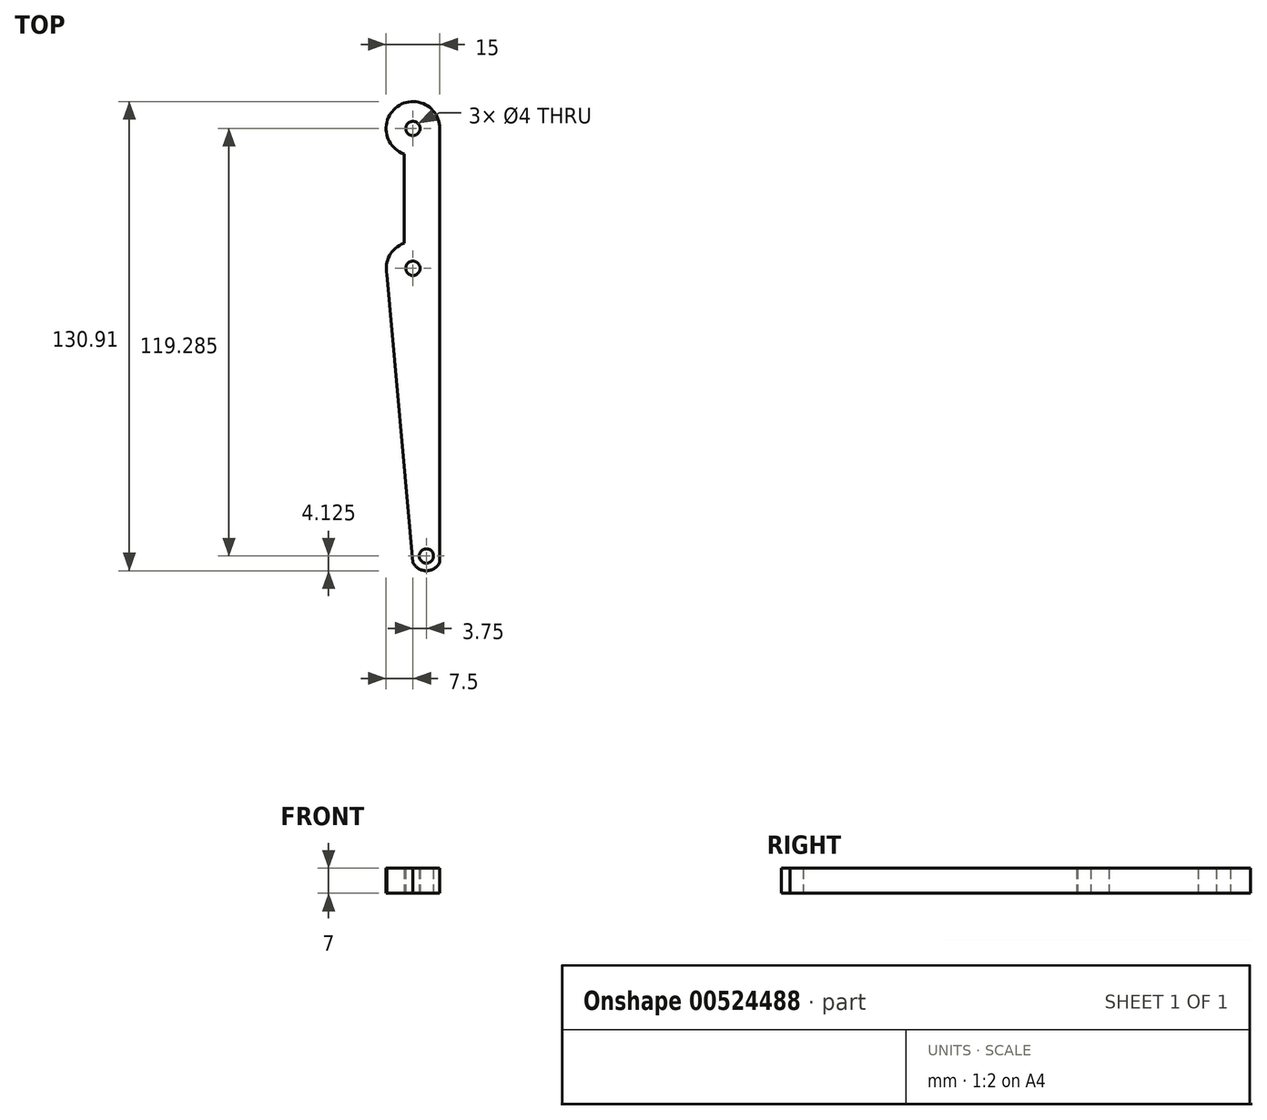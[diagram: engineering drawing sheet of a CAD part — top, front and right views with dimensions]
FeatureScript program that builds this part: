
annotation { "Feature Type Name" : "Feature", "Feature Type Description" : "" }
export const myFeature = defineFeature(function(context is Context, id is Id, definition is map)
    precondition{}
    {
        {
            var Q0;
            Q0=qCreatedBy(makeId("Top.planeOp"),FACE);
            var sketch = newSketch(context, id + "F0", { "sketchPlane" : qUnion([Q0])});
            skArc(sketch, "E0", {"start": v(7.5, 0) * mm, "mid": v(-4.33, 6.12) * mm, "end": v(-2.5, -7.07) * mm});
            skLineSegment(sketch, "E1.top", {"start": v(7.5, -41) * mm, "end": v(7.16, -41) * mm});
            skLineSegment(sketch, "E1.left", {"start": v(7.5, 0) * mm, "end": v(7.5, -41) * mm});
            skLineSegment(sketch, "E1.right", {"start": v(-2.5, -7.07) * mm, "end": v(-2.5, -32.01) * mm});
            skArc(sketch, "E2", {"start": v(-2.5, -32.01) * mm, "mid": v(-6.54, -35.48) * mm, "end": v(-7.22, -40.77) * mm});
            skPoint(sketch, "E3.start.orphan", {"position": v(0, -0.9) * mm});
            skLineSegment(sketch, "E4", {"start": v(7.5, -41) * mm, "end": v(7.5, -121) * mm});
            skPoint(sketch, "E5.second.point", {"position": v(0, -121) * mm});
            skPoint(sketch, "E5.third.point", {"position": v(1.86, -115.62) * mm});
            skLineSegment(sketch, "E6", {"start": v(-7.22, -40.77) * mm, "end": v(0, -121) * mm});
            skCircle(sketch, "E7", {"center": v(3.75, -119.28) * mm, "radius": 2 * mm});
            skArc(sketch, "E8.trimOffspring", {"start": v(0, -121) * mm, "mid": v(3.75, -123.4) * mm, "end": v(7.5, -121) * mm});
            skSolve(sketch);
        }
        {
            var Q0;
            Q0=makeQuery(id+"F0.imprint","IMPRINT",FACE,{"disambiguationData":[TD([[makeQuery(id+"F0.imprint","IMPRINT",EDGE,{"derivedFrom":sQuery(id+"F0.wireOp",EDGE,"E0")}),1.0]])]});
            extrude(context, id + "F1", {"entities" : qUnion([Q0]), "depth" : 7 * mm, "offsetDistance" : 25 * mm});
        }
        {
            var Q0;
            Q0=sQuery(id+"F0.wireOp",VERTEX,"E0.center");
            var Q1;
            Q1=makeQuery(id+"F1.opExtrude","SWEPT_BODY",BODY,{"disambiguationData":[OSD([sQuery(id+"F0.wireOp",EDGE,"E0"),sQuery(id+"F0.wireOp",EDGE,"E1.left"),sQuery(id+"F0.wireOp",EDGE,"E1.right"),sQuery(id+"F0.wireOp",EDGE,"E2"),sQuery(id+"F0.wireOp",EDGE,"E4"),sQuery(id+"F0.wireOp",EDGE,"E6"),sQuery(id+"F0.wireOp",EDGE,"E7"),sQuery(id+"F0.wireOp",EDGE,"E8.trimOffspring")])]});
            hole(context, id + "F2", {"style" : HoleStyle.SIMPLE, "endStyle" : HoleEndStyle.THROUGH, "oppositeDirection" : true, "holeDiameter" : 4 * mm, "isTappedThrough" : true, "tappedDepth" : 12 * mm, "tapClearance" : 3, "locations" : qUnion([Q0]), "scope" : qUnion([Q1])});
        }
        {
            var Q0;
            Q0=sQuery(id+"F0.wireOp",VERTEX,"E2.center");
            var Q1;
            Q1=makeQuery(id+"F1.opExtrude","SWEPT_BODY",BODY,{"disambiguationData":[OSD([sQuery(id+"F0.wireOp",EDGE,"E0"),sQuery(id+"F0.wireOp",EDGE,"E1.left"),sQuery(id+"F0.wireOp",EDGE,"E1.right"),sQuery(id+"F0.wireOp",EDGE,"E2"),sQuery(id+"F0.wireOp",EDGE,"E4"),sQuery(id+"F0.wireOp",EDGE,"E6"),sQuery(id+"F0.wireOp",EDGE,"E7"),sQuery(id+"F0.wireOp",EDGE,"E8.trimOffspring")])]});
            hole(context, id + "F3", {"style" : HoleStyle.SIMPLE, "endStyle" : HoleEndStyle.THROUGH, "oppositeDirection" : true, "holeDiameter" : 4 * mm, "isTappedThrough" : true, "tappedDepth" : 12 * mm, "tapClearance" : 3, "locations" : qUnion([Q0]), "scope" : qUnion([Q1])});
        }
    });
